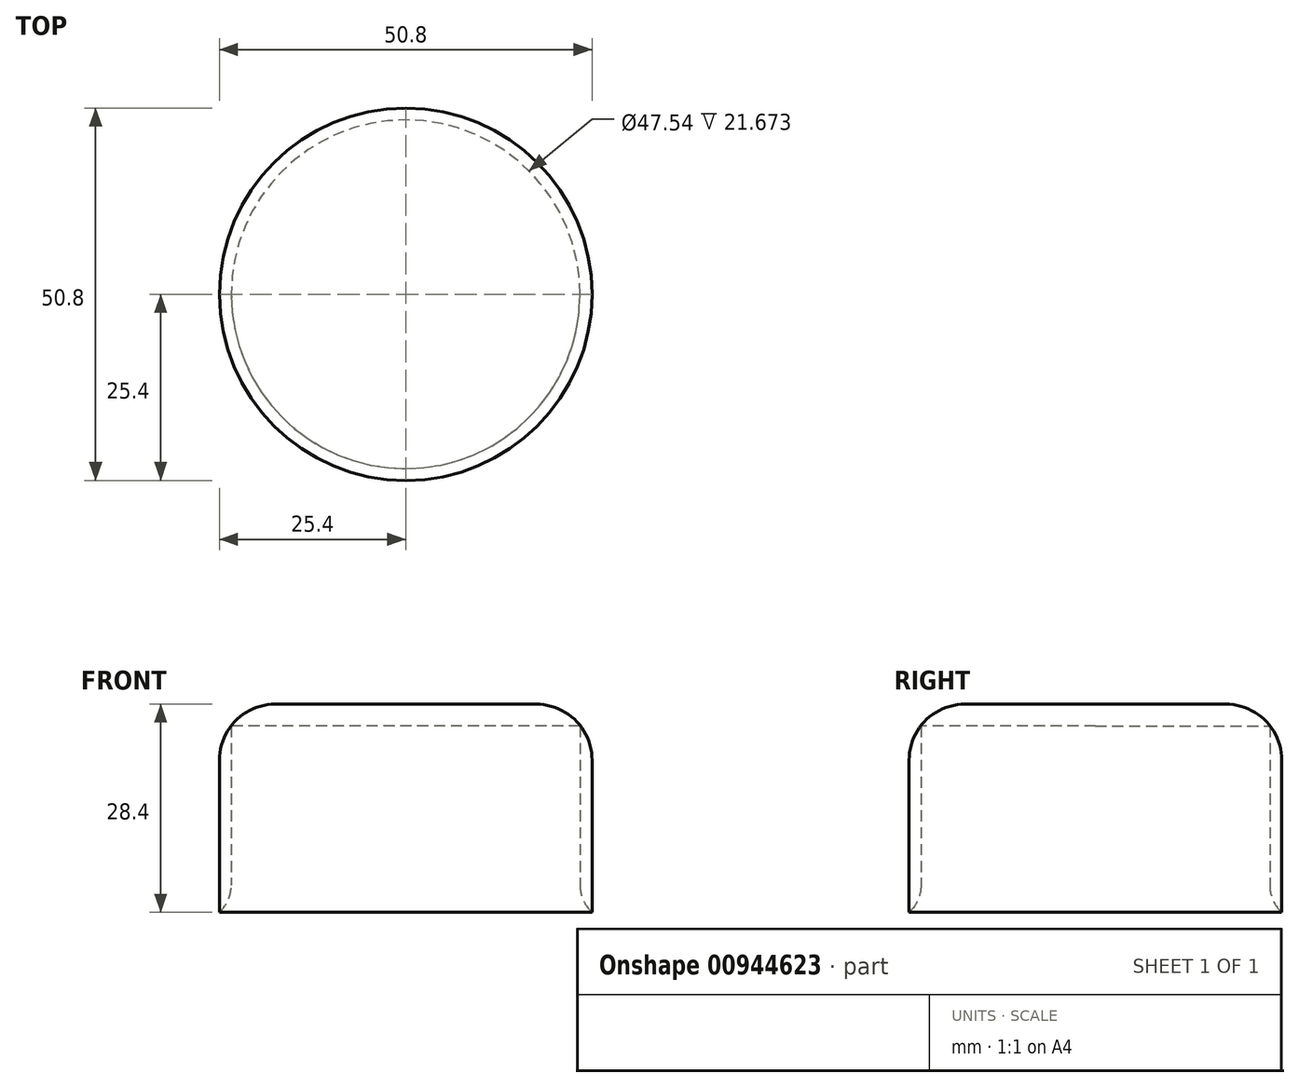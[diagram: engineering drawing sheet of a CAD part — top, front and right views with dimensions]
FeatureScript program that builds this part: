
annotation { "Feature Type Name" : "Feature", "Feature Type Description" : "" }
export const myFeature = defineFeature(function(context is Context, id is Id, definition is map)
    precondition{}
    {
        {
            var Q0;
            Q0=qCreatedBy(makeId("Top.planeOp"),FACE);
            var sketch = newSketch(context, id + "F0", { "sketchPlane" : qUnion([Q0])});
            skCircle(sketch, "E0", {"center": v(0, 0) * mm, "radius": 25.4 * mm});
            skCircle(sketch, "E1", {"center": v(0, 0) * mm, "radius": 23.77 * mm});
            skSolve(sketch);
        }
        {
            var Q0;
            Q0 = qSketchRegion(id + "F0", true);
            extrude(context, id + "F1", {"entities" : qUnion([Q0]), "depth" : 25.4 * mm, "offsetDistance" : 25.4 * mm});
        }
        {
            var Q0;
            Q0=makeQuery(id+"F1.opExtrude","CAP_FACE",FACE,{"disambiguationData":[OSD([sQuery(id+"F0.wireOp",EDGE,"E0"),sQuery(id+"F0.wireOp",EDGE,"E1")])],"isStart":false});
            var sketch = newSketch(context, id + "F2", { "sketchPlane" : qUnion([Q0])});
            skCircle(sketch, "E2", {"center": v(0, 0) * mm, "radius": 25.4 * mm});
            skSolve(sketch);
        }
        {
            var Q0;
            Q0 = qSketchRegion(id + "F2", true);
            var Q1;
            Q1=makeQuery(id+"F2.imprint","IMPRINT",FACE,{"disambiguationData":[TD([[makeQuery(id+"F2.imprint","IMPRINT",EDGE,{"derivedFrom":sQuery(id+"F2.wireOp",EDGE,"E2")}),1.0]])]});
            extrude(context, id + "F3", {"entities" : qUnion([Q0, Q1]), "operationType" : NewBodyOperationType.ADD, "depth" : 3 * mm, "offsetDistance" : 25.4 * mm});
        }
        {
            var Q0;
            Q0=makeQuery(id+"F3.opExtrude","CAP_EDGE",EDGE,{"disambiguationData":[OSD([sQuery(id+"F2.wireOp",EDGE,"E2")])],"isStart":false});
            fillet(context, id + "F4", {"entities" : qUnion([Q0]), "radius" : 7.62 * mm, "tangentPropagation" : true, "allowEdgeOverflow" : false});
        }
        {
            var Q0;
            Q0=makeQuery(id+"F1.opExtrude","CAP_EDGE",EDGE,{"disambiguationData":[OSD([sQuery(id+"F0.wireOp",EDGE,"E1")])],"isStart":true});
            fillet(context, id + "F5", {"entities" : qUnion([Q0]), "radius" : 5.08 * mm, "tangentPropagation" : true, "allowEdgeOverflow" : false});
        }
    });
